# Revit family: Storage-Teknion-CESRUX_Recycling_Disposal_Unit_XL_Bins-R2023
name_source: partatom
category: Furniture
units: mm (PartAtom-declared; Revit-internal decimal feet)

## family parameters
Always vertical = Yes
Cut with Voids When Loaded = No
Enable Cutting in Views = No
OmniClass Number = 23.40.20.00
OmniClass Title = General Furniture and Specialties
Render Appearance Source = Family Geometry
Room Calculation Point = No
Shared = Yes
Work Plane-Based = No

## types (2) — shared parameters
Assembly Code = E2020200
Manufacturer = Teknion
Manufacturer Fax = 416.661.4586
Part Number = CESRUX
Product Documentation Link = https://www.teknion.com
Product Line = Storage Cabinets
Product Page URL = https://www.teknion.com
Series = Expansion Casework+
Sustainability Data = https://www.teknion.com
URL = www.teknion.com
Unit Weight URL = http://www.teknion.com
Warranty = http://www.teknion.com
zero-valued in all types: Default Elevation

## per-type parameters (varying)
| type | 2D - 3 Bins | Cut - 2 Doors | Cut - 3 Doors | Cut - Divider - 1 | Cut - Divider - 2 | Cut - Divider - 3 | Cut-Out - 3 Bins | D - Dual | Description | Dim 1 | Divider 1 | Divider 2 | Divider 3 | Hidden - Divider 1 | Hidden - Divider 2 | Hidden - Divider 3 | Model | T - Triple |
| Dual Configuration | No | 2.5 " | 0.3 " | 0.3 " | 3 " | 0.3 " | 0.2 " | Yes | Recycling/Disposal Unit - XL Bins, Dual Configuration | 6 " | No | Yes | No | Yes | No | Yes | CESRUXD________ | No |
| Triple Configuration | Yes | 0.3 " | 2.5 " | 3 " | 0.3 " | 3 " | 1.5 " | No | Recycling/Disposal Unit - XL Bins, Triple Configuration | 9 " | Yes | No | Yes | No | Yes | No | CESRUXT________ | Yes |

## geometry (parser evidence)
native form markers: Sweep x7
no freeform markers — native parametric forms only
